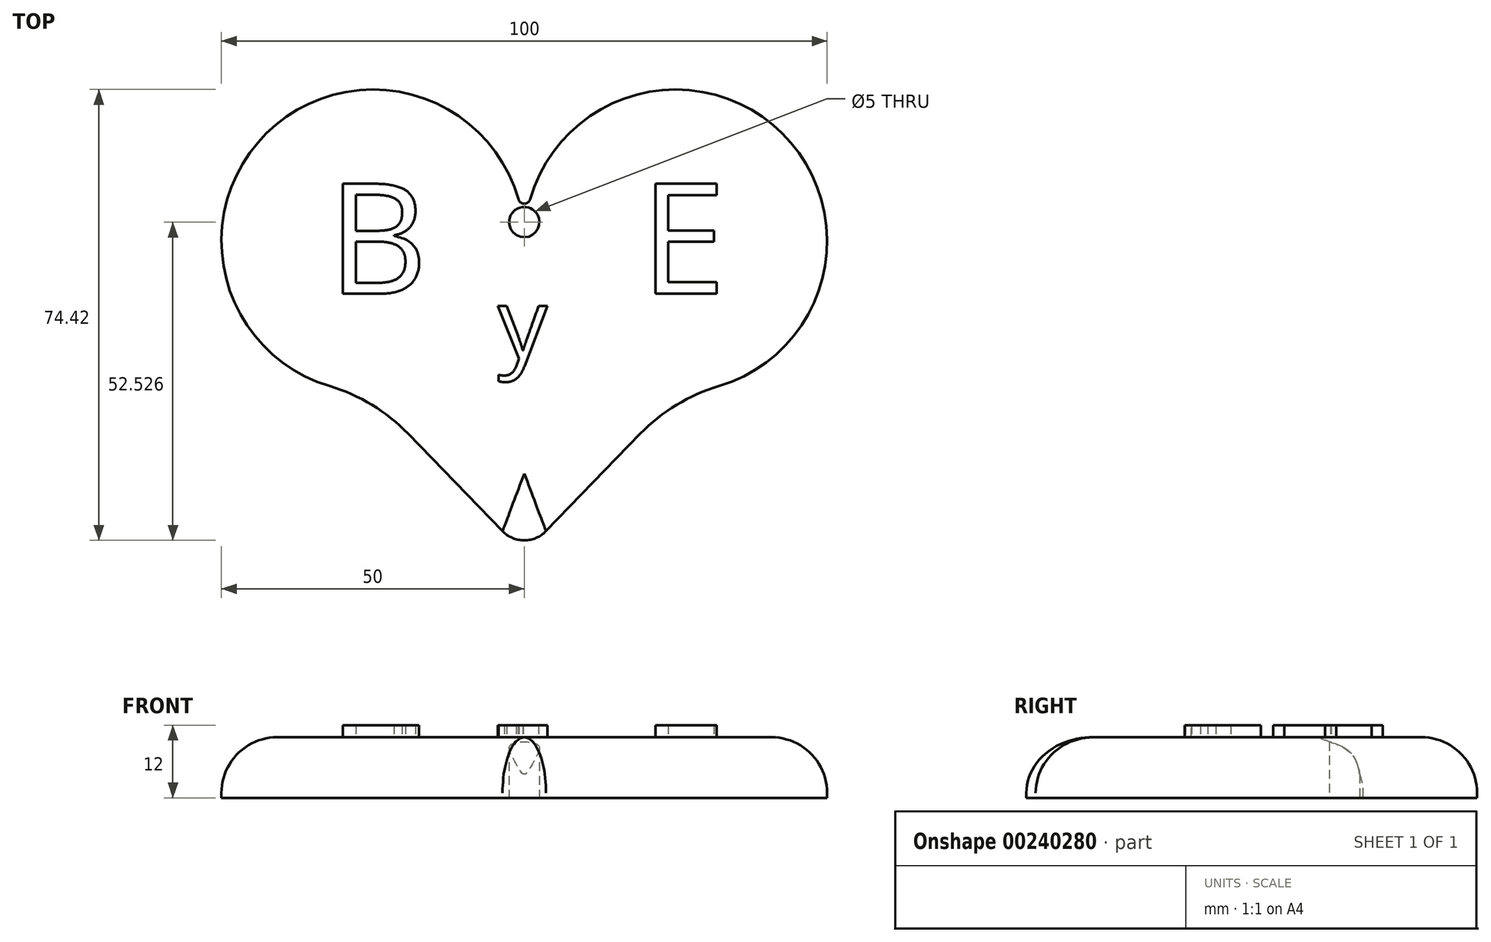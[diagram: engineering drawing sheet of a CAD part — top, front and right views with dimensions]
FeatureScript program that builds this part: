
annotation { "Feature Type Name" : "Feature", "Feature Type Description" : "" }
export const myFeature = defineFeature(function(context is Context, id is Id, definition is map)
    precondition{}
    {
        {
            var Q0;
            Q0=qCreatedBy(makeId("Top.planeOp"),FACE);
            var sketch = newSketch(context, id + "F0", { "sketchPlane" : qUnion([Q0])});
            skLineSegment(sketch, "E0", {"start": v(0, 0) * mm, "end": v(-50, 0) * mm, "construction": true});
            skArc(sketch, "E1", {"start": v(-0.96, 6.87) * mm, "mid": v(-42.58, 17.78) * mm, "end": v(-32.14, -23.96) * mm});
            skLineSegment(sketch, "E2", {"start": v(0, 0) * mm, "end": v(50, 0) * mm, "construction": true});
            skArc(sketch, "E3", {"start": v(32.14, -23.96) * mm, "mid": v(42.58, 17.78) * mm, "end": v(0.96, 6.87) * mm});
            skLineSegment(sketch, "E4", {"start": v(0, 0) * mm, "end": v(0, -51.6) * mm, "construction": true});
            skLineSegment(sketch, "E5", {"start": v(-3.6, -47.9) * mm, "end": v(-19.16, -31.84) * mm});
            skLineSegment(sketch, "E6", {"start": v(3.6, -47.9) * mm, "end": v(19.16, -31.84) * mm});
            skPoint(sketch, "E7.visualSharp", {"position": v(-25.8, -24.99) * mm});
            skArc(sketch, "E7.filletArc", {"start": v(-19.16, -31.84) * mm, "mid": v(-25.14, -27.06) * mm, "end": v(-32.14, -23.96) * mm});
            skPoint(sketch, "E8.visualSharp", {"position": v(25.8, -24.99) * mm});
            skArc(sketch, "E8.filletArc", {"start": v(32.14, -23.96) * mm, "mid": v(25.14, -27.06) * mm, "end": v(19.16, -31.84) * mm});
            skPoint(sketch, "E9.visualSharp", {"position": v(0, -51.6) * mm});
            skArc(sketch, "E9.filletArc", {"start": v(-3.6, -47.9) * mm, "mid": v(0, -49.42) * mm, "end": v(3.6, -47.9) * mm});
            skPoint(sketch, "E10.visualSharp", {"position": v(0, 0) * mm});
            skArc(sketch, "E10.filletArc", {"start": v(-0.96, 6.87) * mm, "mid": v(0, 6.14) * mm, "end": v(0.96, 6.87) * mm});
            skSolve(sketch);
        }
        {
            var Q0;
            Q0=makeQuery(id+"F0.imprint","IMPRINT",FACE,{"disambiguationData":[TD([[makeQuery(id+"F0.imprint","IMPRINT",EDGE,{"derivedFrom":sQuery(id+"F0.wireOp",EDGE,"E1")}),1.0]])]});
            extrude(context, id + "F1", {"entities" : qUnion([Q0]), "depth" : 10 * mm});
        }
        {
            var Q0;
            Q0=makeQuery(id+"F1.opExtrude","CAP_FACE",FACE,{"disambiguationData":[OSD([sQuery(id+"F0.wireOp",EDGE,"E1"),sQuery(id+"F0.wireOp",EDGE,"E3"),sQuery(id+"F0.wireOp",EDGE,"E5"),sQuery(id+"F0.wireOp",EDGE,"E6"),sQuery(id+"F0.wireOp",EDGE,"E7.filletArc"),sQuery(id+"F0.wireOp",EDGE,"E8.filletArc"),sQuery(id+"F0.wireOp",EDGE,"E9.filletArc"),sQuery(id+"F0.wireOp",EDGE,"E10.filletArc")])],"isStart":false});
            var sketch = newSketch(context, id + "F2", { "sketchPlane" : qUnion([Q0])});
            skText(sketch, "E11", { "text": "B", "fontName": "OpenSans-Regular.ttf"});
            skText(sketch, "E12", { "text": "y\n", "fontName": "OpenSans-Regular.ttf"});
            skText(sketch, "E13", { "text": "E", "fontName": "OpenSans-Regular.ttf"});
            const initialGuessF2  = {"E11": [-0.03243, -0.0087, 1, 0, 0.0183], "E12": [-0.00437, -0.0194, 1, 0, 0.0117], "E13": [0.01917, -0.0087, 1, 0, 0.01831]};
            skSetInitialGuess(sketch, initialGuessF2);
            skSolve(sketch);
        }
        {
            var Q0;
            Q0 = qSketchRegion(id + "F2", true);
            extrude(context, id + "F3", {"entities" : qUnion([Q0]), "operationType" : NewBodyOperationType.ADD, "depth" : 2 * mm});
        }
        {
            var Q0;
            Q0=makeQuery(id+"F1.opExtrude","CAP_EDGE",EDGE,{"disambiguationData":[OSD([sQuery(id+"F0.wireOp",EDGE,"E1")])],"isStart":false});
            fillet(context, id + "F4", {"entities" : qUnion([Q0]), "radius" : 9.2 * mm, "tangentPropagation" : true, "allowEdgeOverflow" : false});
        }
        {
            var Q0;
            Q0=makeQuery(id+"F1.opExtrude","CAP_FACE",FACE,{"disambiguationData":[OSD([sQuery(id+"F0.wireOp",EDGE,"E1"),sQuery(id+"F0.wireOp",EDGE,"E3"),sQuery(id+"F0.wireOp",EDGE,"E5"),sQuery(id+"F0.wireOp",EDGE,"E6"),sQuery(id+"F0.wireOp",EDGE,"E7.filletArc"),sQuery(id+"F0.wireOp",EDGE,"E8.filletArc"),sQuery(id+"F0.wireOp",EDGE,"E9.filletArc"),sQuery(id+"F0.wireOp",EDGE,"E10.filletArc")])],"isStart":true});
            var sketch = newSketch(context, id + "F5", { "sketchPlane" : qUnion([Q0])});
            skCircle(sketch, "E14", {"center": v(0, -3.1) * mm, "radius": 2.5 * mm});
            skSolve(sketch);
        }
        {
            var Q0;
            Q0=makeQuery(id+"F5.imprint","IMPRINT",FACE,{"disambiguationData":[TD([[makeQuery(id+"F5.imprint","IMPRINT",EDGE,{"derivedFrom":sQuery(id+"F5.wireOp",EDGE,"E14")}),1.0]])]});
            extrude(context, id + "F6", {"entities" : qUnion([Q0]), "operationType" : NewBodyOperationType.REMOVE, "oppositeDirection" : true, "depth" : 28.7 * mm});
        }
    });
